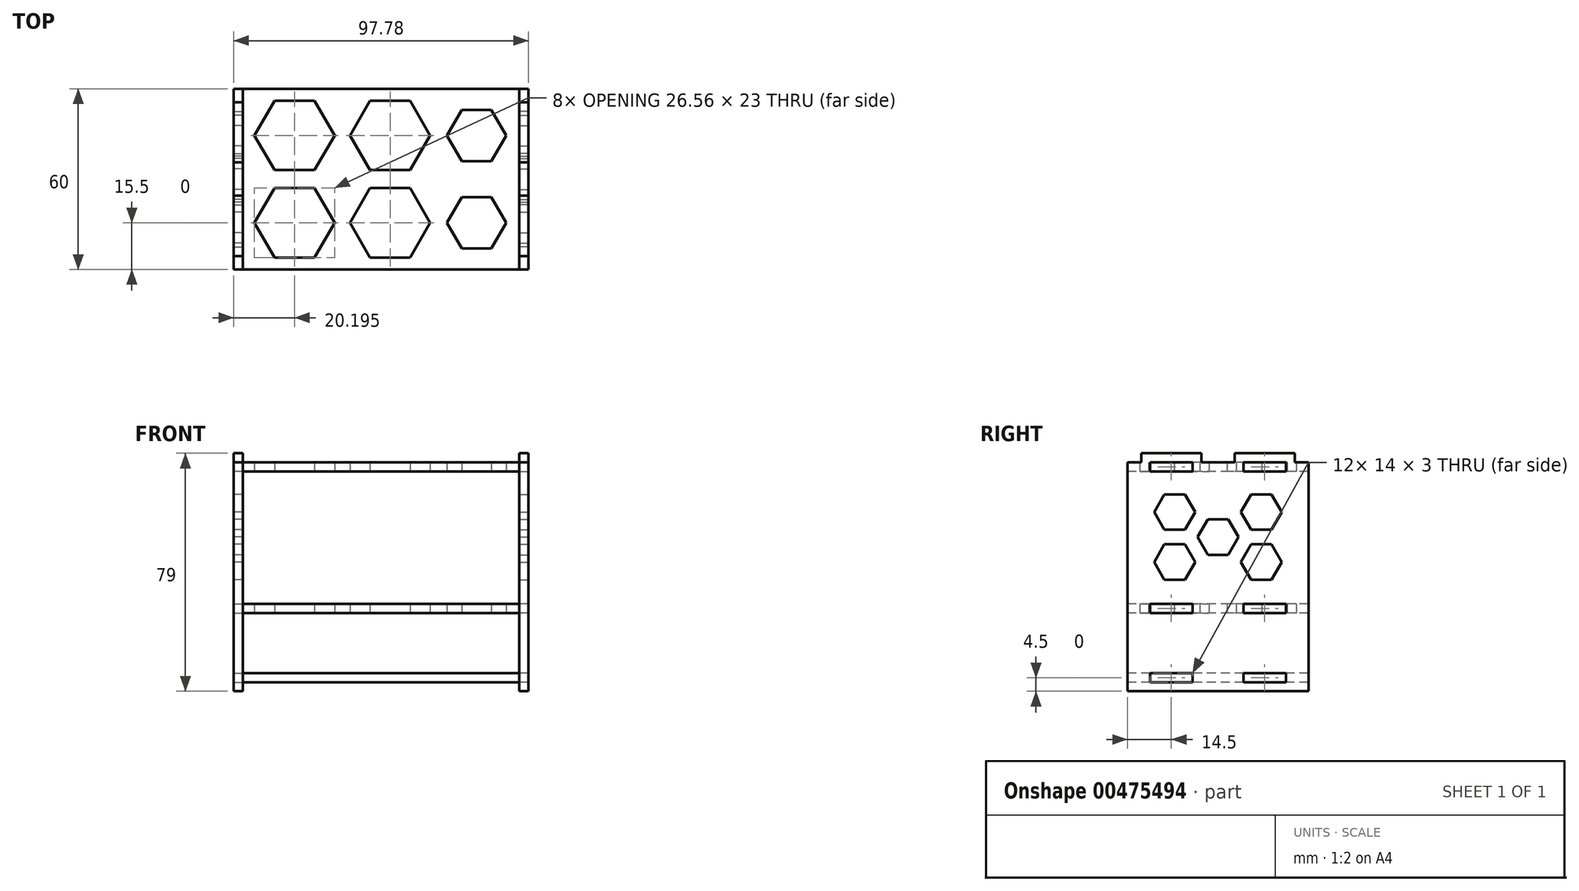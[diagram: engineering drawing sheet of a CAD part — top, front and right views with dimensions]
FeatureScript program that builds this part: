
annotation { "Feature Type Name" : "Feature", "Feature Type Description" : "" }
export const myFeature = defineFeature(function(context is Context, id is Id, definition is map)
    precondition{}
    {
        {
            assignVariable(context, id + "F0", {"name" : "x", "anyValue" : 3});
        }
        {
            var Q0;
            Q0=qCreatedBy(makeId("Top.planeOp"),FACE);
            var sketch = newSketch(context, id + "F1", { "sketchPlane" : qUnion([Q0])});
            skLineSegment(sketch, "E0.bottom", {"start": v(45.9, 30) * mm, "end": v(-45.9, 30) * mm});
            skLineSegment(sketch, "E0.top", {"start": v(45.9, -30) * mm, "end": v(-45.9, -30) * mm});
            skPoint(sketch, "E0.middle", {"position": v(0, 0) * mm});
            skCircle(sketch, "E1", {"center": v(-28.7, 14.5) * mm, "radius": 11.5 * mm, "construction": true});
            skCircle(sketch, "E2", {"center": v(3, 14.5) * mm, "radius": 11.5 * mm, "construction": true});
            skCircle(sketch, "E3", {"center": v(31.7, 14.5) * mm, "radius": 8.5 * mm, "construction": true});
            skPoint(sketch, "E4", {"position": v(-48.9, 0) * mm});
            skLineSegment(sketch, "E5", {"start": v(-48.9, 14.5) * mm, "end": v(48.9, 14.5) * mm, "construction": true});
            skLineSegment(sketch, "E6", {"start": v(-17.2, 14.5) * mm, "end": v(-8.5, 14.5) * mm, "construction": true});
            skLineSegment(sketch, "E7", {"start": v(14.5, 14.5) * mm, "end": v(23.2, 14.5) * mm, "construction": true});
            skLineSegment(sketch, "E8", {"start": v(-40.2, 14.5) * mm, "end": v(-48.9, 14.5) * mm, "construction": true});
            skLineSegment(sketch, "E9", {"start": v(40.2, 14.5) * mm, "end": v(48.9, 14.5) * mm, "construction": true});
            skLineSegment(sketch, "E10.bottom", {"start": v(-48.9, 8.5) * mm, "end": v(-45.9, 8.5) * mm});
            skLineSegment(sketch, "E10.top", {"start": v(-48.9, 22.5) * mm, "end": v(-45.9, 22.5) * mm});
            skLineSegment(sketch, "E10.left", {"start": v(-48.9, 8.5) * mm, "end": v(-48.9, 22.5) * mm});
            skLineSegment(sketch, "E11", {"start": v(-45.9, 30) * mm, "end": v(-45.9, 22.5) * mm});
            skLineSegment(sketch, "E12.MirrorCS", {"start": v(-48.9, -8.5) * mm, "end": v(-45.9, -8.5) * mm});
            skLineSegment(sketch, "E13.MirrorCS", {"start": v(-48.9, -22.5) * mm, "end": v(-45.9, -22.5) * mm});
            skLineSegment(sketch, "E14.MirrorCS", {"start": v(-48.9, -8.5) * mm, "end": v(-48.9, -22.5) * mm});
            skLineSegment(sketch, "E15.trimOffspring", {"start": v(-45.9, -22.5) * mm, "end": v(-45.9, -30) * mm});
            skPoint(sketch, "E16.MirrorCS.end.orphan", {"position": v(-45.9, -22.5) * mm});
            skPoint(sketch, "E16.MirrorCS.start.orphan", {"position": v(-45.9, -8.5) * mm});
            skLineSegment(sketch, "E17.trimOffspring", {"start": v(-45.9, 8.5) * mm, "end": v(-45.9, -8.5) * mm});
            skPoint(sketch, "E18.orphan", {"position": v(-48.9, 30) * mm});
            skPoint(sketch, "E19.orphan", {"position": v(-48.9, -30) * mm});
            skPoint(sketch, "E20.MirrorP", {"position": v(48.9, 0) * mm});
            skLineSegment(sketch, "E21.MirrorCS", {"start": v(48.9, 8.5) * mm, "end": v(48.9, 22.5) * mm});
            skLineSegment(sketch, "E22.MirrorCS", {"start": v(45.9, 8.5) * mm, "end": v(45.9, -8.5) * mm});
            skPoint(sketch, "E23.MirrorP", {"position": v(45.9, -8.5) * mm});
            skLineSegment(sketch, "E24.MirrorCS", {"start": v(48.9, 8.5) * mm, "end": v(45.9, 8.5) * mm});
            skLineSegment(sketch, "E25.MirrorCS", {"start": v(48.9, -8.5) * mm, "end": v(45.9, -8.5) * mm});
            skLineSegment(sketch, "E26.MirrorCS", {"start": v(48.9, -22.5) * mm, "end": v(45.9, -22.5) * mm});
            skPoint(sketch, "E27.MirrorP", {"position": v(45.9, -22.5) * mm});
            skLineSegment(sketch, "E28.MirrorCS", {"start": v(48.9, 22.5) * mm, "end": v(45.9, 22.5) * mm});
            skLineSegment(sketch, "E29.MirrorCS", {"start": v(48.9, -8.5) * mm, "end": v(48.9, -22.5) * mm});
            skLineSegment(sketch, "E30.MirrorCS", {"start": v(45.9, -22.5) * mm, "end": v(45.9, -30) * mm});
            skLineSegment(sketch, "E31.MirrorCS", {"start": v(45.9, 30) * mm, "end": v(45.9, 22.5) * mm});
            skPoint(sketch, "E32.orphan", {"position": v(48.9, 30) * mm});
            skPoint(sketch, "E33.orphan", {"position": v(48.9, -30) * mm});
            skLineSegment(sketch, "E34.0", {"start": v(-22.06, 26) * mm, "end": v(-15.42, 14.5) * mm});
            skLineSegment(sketch, "E34.1", {"start": v(-15.42, 14.5) * mm, "end": v(-22.06, 3) * mm});
            skLineSegment(sketch, "E34.2", {"start": v(-22.06, 3) * mm, "end": v(-35.33, 3) * mm});
            skLineSegment(sketch, "E34.3", {"start": v(-35.33, 3) * mm, "end": v(-41.97, 14.5) * mm});
            skLineSegment(sketch, "E34.4", {"start": v(-41.97, 14.5) * mm, "end": v(-35.33, 26) * mm});
            skLineSegment(sketch, "E34.5", {"start": v(-35.33, 26) * mm, "end": v(-22.06, 26) * mm});
            skPoint(sketch, "E34.0.midPoint", {"position": v(-18.74, 20.25) * mm});
            skLineSegment(sketch, "E35.0", {"start": v(9.64, 26) * mm, "end": v(16.28, 14.5) * mm});
            skLineSegment(sketch, "E35.1", {"start": v(16.28, 14.5) * mm, "end": v(9.64, 3) * mm});
            skLineSegment(sketch, "E35.2", {"start": v(9.64, 3) * mm, "end": v(-3.64, 3) * mm});
            skLineSegment(sketch, "E35.3", {"start": v(-3.64, 3) * mm, "end": v(-10.28, 14.5) * mm});
            skLineSegment(sketch, "E35.4", {"start": v(-10.28, 14.5) * mm, "end": v(-3.64, 26) * mm});
            skLineSegment(sketch, "E35.5", {"start": v(-3.64, 26) * mm, "end": v(9.64, 26) * mm});
            skPoint(sketch, "E35.0.midPoint", {"position": v(12.96, 20.25) * mm});
            skLineSegment(sketch, "E36.0", {"start": v(36.6, 23) * mm, "end": v(41.51, 14.5) * mm});
            skLineSegment(sketch, "E36.1", {"start": v(41.51, 14.5) * mm, "end": v(36.6, 6) * mm});
            skLineSegment(sketch, "E36.2", {"start": v(36.6, 6) * mm, "end": v(26.79, 6) * mm});
            skLineSegment(sketch, "E36.3", {"start": v(26.79, 6) * mm, "end": v(21.88, 14.5) * mm});
            skLineSegment(sketch, "E36.4", {"start": v(21.88, 14.5) * mm, "end": v(26.79, 23) * mm});
            skLineSegment(sketch, "E36.5", {"start": v(26.79, 23) * mm, "end": v(36.6, 23) * mm});
            skPoint(sketch, "E36.0.midPoint", {"position": v(39.06, 18.75) * mm});
            skLineSegment(sketch, "E37.MirrorCS", {"start": v(36.6, -6) * mm, "end": v(26.79, -6) * mm});
            skLineSegment(sketch, "E38.MirrorCS", {"start": v(26.79, -23) * mm, "end": v(36.6, -23) * mm});
            skLineSegment(sketch, "E39.MirrorCS", {"start": v(-22.06, -3) * mm, "end": v(-35.33, -3) * mm});
            skLineSegment(sketch, "E40.MirrorCS", {"start": v(-17.2, -14.5) * mm, "end": v(-8.5, -14.5) * mm, "construction": true});
            skLineSegment(sketch, "E41.MirrorCS", {"start": v(9.64, -3) * mm, "end": v(-3.64, -3) * mm});
            skLineSegment(sketch, "E42.MirrorCS", {"start": v(21.88, -14.5) * mm, "end": v(26.79, -23) * mm});
            skCircle(sketch, "E43.MirrorC", {"center": v(-28.7, -14.5) * mm, "radius": 11.5 * mm, "construction": true});
            skLineSegment(sketch, "E44.MirrorCS", {"start": v(9.64, -26) * mm, "end": v(16.28, -14.5) * mm});
            skLineSegment(sketch, "E45.MirrorCS", {"start": v(36.6, -23) * mm, "end": v(41.51, -14.5) * mm});
            skLineSegment(sketch, "E46.MirrorCS", {"start": v(-22.06, -26) * mm, "end": v(-15.42, -14.5) * mm});
            skCircle(sketch, "E47.MirrorC", {"center": v(3, -14.5) * mm, "radius": 11.5 * mm, "construction": true});
            skCircle(sketch, "E48.MirrorC", {"center": v(31.7, -14.5) * mm, "radius": 8.5 * mm, "construction": true});
            skLineSegment(sketch, "E49.MirrorCS", {"start": v(14.5, -14.5) * mm, "end": v(23.2, -14.5) * mm, "construction": true});
            skLineSegment(sketch, "E50.MirrorCS", {"start": v(-3.64, -3) * mm, "end": v(-10.28, -14.5) * mm});
            skLineSegment(sketch, "E51.MirrorCS", {"start": v(-3.64, -26) * mm, "end": v(9.64, -26) * mm});
            skLineSegment(sketch, "E52.MirrorCS", {"start": v(-41.97, -14.5) * mm, "end": v(-35.33, -26) * mm});
            skPoint(sketch, "E53.MirrorP", {"position": v(39.06, -18.75) * mm});
            skLineSegment(sketch, "E54.MirrorCS", {"start": v(-15.42, -14.5) * mm, "end": v(-22.06, -3) * mm});
            skLineSegment(sketch, "E55.MirrorCS", {"start": v(-35.33, -3) * mm, "end": v(-41.97, -14.5) * mm});
            skPoint(sketch, "E56.MirrorP", {"position": v(-18.74, -20.25) * mm});
            skPoint(sketch, "E57.MirrorP", {"position": v(12.96, -20.25) * mm});
            skLineSegment(sketch, "E58.MirrorCS", {"start": v(-35.33, -26) * mm, "end": v(-22.06, -26) * mm});
            skLineSegment(sketch, "E59.MirrorCS", {"start": v(-10.28, -14.5) * mm, "end": v(-3.64, -26) * mm});
            skLineSegment(sketch, "E60.MirrorCS", {"start": v(26.79, -6) * mm, "end": v(21.88, -14.5) * mm});
            skLineSegment(sketch, "E61.MirrorCS", {"start": v(16.28, -14.5) * mm, "end": v(9.64, -3) * mm});
            skLineSegment(sketch, "E62.MirrorCS", {"start": v(41.51, -14.5) * mm, "end": v(36.6, -6) * mm});
            skSolve(sketch);
        }
        {
            var Q0;
            Q0=makeQuery(id+"F1.imprint","IMPRINT",FACE,{"disambiguationData":[TD([[makeQuery(id+"F1.imprint","IMPRINT",EDGE,{"derivedFrom":sQuery(id+"F1.wireOp",EDGE,"E0.bottom")}),1.0]])]});
            extrude(context, id + "F2", {"entities" : qUnion([Q0]), "depth" : 50 * mm});
        }
        {
            var Q0;
            Q0 = qSketchRegion(id + "F1", true);
            extrude(context, id + "F3", {"entities" : qUnion([Q0]), "operationType" : NewBodyOperationType.REMOVE, "depth" : (50 - getVariable(context, 'x')) * mm});
        }
        {
            var Q0;
            Q0 = qSketchRegion(id + "F1", true);
            extrude(context, id + "F4", {"entities" : qUnion([Q0]), "depth" : (getVariable(context, 'x')) * mm});
        }
        {
            var Q0;
            Q0=makeQuery(id+"F1.imprint","IMPRINT",FACE,{"disambiguationData":[TD([[makeQuery(id+"F1.imprint","IMPRINT",EDGE,{"derivedFrom":sQuery(id+"F1.wireOp",EDGE,"E0.bottom")}),1.0]])]});
            var sketch = newSketch(context, id + "F5", { "sketchPlane" : qUnion([Q0])});
            skPoint(sketch, "E63", {"position": v(-45.9, -30) * mm});
            skLineSegment(sketch, "E64", {"start": v(-45.9, -30) * mm, "end": v(-45.9, -22.5) * mm});
            skLineSegment(sketch, "E65", {"start": v(-45.9, -22.5) * mm, "end": v(-48.9, -22.5) * mm});
            skLineSegment(sketch, "E66", {"start": v(-48.9, -22.5) * mm, "end": v(-48.9, -8.5) * mm});
            skLineSegment(sketch, "E67", {"start": v(-48.9, -8.5) * mm, "end": v(-45.9, -8.5) * mm});
            skLineSegment(sketch, "E68", {"start": v(-45.9, -8.5) * mm, "end": v(-45.9, 0) * mm});
            skLineSegment(sketch, "E69", {"start": v(-45.9, -30) * mm, "end": v(0, -30) * mm});
            skLineSegment(sketch, "E70.MirrorCS", {"start": v(45.9, -30) * mm, "end": v(45.9, -22.5) * mm});
            skLineSegment(sketch, "E71.MirrorCS", {"start": v(45.9, -22.5) * mm, "end": v(48.9, -22.5) * mm});
            skLineSegment(sketch, "E72.MirrorCS", {"start": v(48.9, -8.5) * mm, "end": v(45.9, -8.5) * mm});
            skLineSegment(sketch, "E73.MirrorCS", {"start": v(45.9, -8.5) * mm, "end": v(45.9, 0) * mm});
            skPoint(sketch, "E74.MirrorP", {"position": v(45.9, -30) * mm});
            skLineSegment(sketch, "E75.MirrorCS", {"start": v(45.9, -30) * mm, "end": v(0, -30) * mm});
            skLineSegment(sketch, "E76.MirrorCS", {"start": v(48.9, -22.5) * mm, "end": v(48.9, -8.5) * mm});
            skLineSegment(sketch, "E77.MirrorCS", {"start": v(48.9, 8.5) * mm, "end": v(45.9, 8.5) * mm});
            skLineSegment(sketch, "E78.MirrorCS", {"start": v(-45.9, 30) * mm, "end": v(-45.9, 22.5) * mm});
            skLineSegment(sketch, "E79.MirrorCS", {"start": v(-45.9, 22.5) * mm, "end": v(-48.9, 22.5) * mm});
            skLineSegment(sketch, "E80.MirrorCS", {"start": v(45.9, 22.5) * mm, "end": v(48.9, 22.5) * mm});
            skLineSegment(sketch, "E81.MirrorCS", {"start": v(-48.9, 8.5) * mm, "end": v(-45.9, 8.5) * mm});
            skLineSegment(sketch, "E82.MirrorCS", {"start": v(45.9, 30) * mm, "end": v(45.9, 22.5) * mm});
            skLineSegment(sketch, "E83.MirrorCS", {"start": v(45.9, 8.5) * mm, "end": v(45.9, 0) * mm});
            skLineSegment(sketch, "E84.MirrorCS", {"start": v(-45.9, 8.5) * mm, "end": v(-45.9, 0) * mm});
            skPoint(sketch, "E85.MirrorP", {"position": v(-45.9, 30) * mm});
            skPoint(sketch, "E86.MirrorP", {"position": v(45.9, 30) * mm});
            skLineSegment(sketch, "E87.MirrorCS", {"start": v(48.9, 22.5) * mm, "end": v(48.9, 8.5) * mm});
            skLineSegment(sketch, "E88.MirrorCS", {"start": v(45.9, 30) * mm, "end": v(0, 30) * mm});
            skLineSegment(sketch, "E89.MirrorCS", {"start": v(-48.9, 22.5) * mm, "end": v(-48.9, 8.5) * mm});
            skLineSegment(sketch, "E90.MirrorCS", {"start": v(-45.9, 30) * mm, "end": v(0, 30) * mm});
            skSolve(sketch);
        }
        {
            var Q0;
            Q0 = qSketchRegion(id + "F5", true);
            extrude(context, id + "F6", {"entities" : qUnion([Q0]), "oppositeDirection" : true, "depth" : 23 * mm});
        }
        {
            var Q0;
            Q0 = qSketchRegion(id + "F5", true);
            extrude(context, id + "F7", {"entities" : qUnion([Q0]), "operationType" : NewBodyOperationType.REMOVE, "oppositeDirection" : true, "depth" : (23 - getVariable(context, 'x')) * mm});
        }
        {
            var Q0;
            Q0=makeQuery(id+"F4.opExtrude","SWEPT_FACE",FACE,{"disambiguationData":[OSD([sQuery(id+"F1.wireOp",EDGE,"E14.MirrorCS")])]});
            var sketch = newSketch(context, id + "F8", { "sketchPlane" : qUnion([Q0])});
            skLineSegment(sketch, "E91", {"start": v(30, -23) * mm, "end": v(30, 50) * mm});
            skLineSegment(sketch, "E92", {"start": v(30, 50) * mm, "end": v(25.5, 50) * mm});
            skLineSegment(sketch, "E93", {"start": v(25.5, 50) * mm, "end": v(25.5, 53) * mm});
            skLineSegment(sketch, "E94", {"start": v(25.5, 53) * mm, "end": v(5.5, 53) * mm});
            skLineSegment(sketch, "E95", {"start": v(5.5, 53) * mm, "end": v(5.5, 50) * mm});
            skLineSegment(sketch, "E96", {"start": v(5.5, 50) * mm, "end": v(0, 50) * mm});
            skLineSegment(sketch, "E97", {"start": v(30, -23) * mm, "end": v(30, -26) * mm});
            skLineSegment(sketch, "E98", {"start": v(30, -26) * mm, "end": v(0, -26) * mm});
            skLineSegment(sketch, "E99.bottom", {"start": v(8.5, -23) * mm, "end": v(22.5, -23) * mm});
            skLineSegment(sketch, "E99.top", {"start": v(8.5, -20) * mm, "end": v(22.5, -20) * mm});
            skLineSegment(sketch, "E99.left", {"start": v(8.5, -23) * mm, "end": v(8.5, -20) * mm});
            skLineSegment(sketch, "E99.right", {"start": v(22.5, -23) * mm, "end": v(22.5, -20) * mm});
            skLineSegment(sketch, "E100.bottom", {"start": v(8.5, 0) * mm, "end": v(22.5, 0) * mm});
            skLineSegment(sketch, "E100.top", {"start": v(8.5, 3) * mm, "end": v(22.5, 3) * mm});
            skLineSegment(sketch, "E100.left", {"start": v(8.5, 0) * mm, "end": v(8.5, 3) * mm});
            skLineSegment(sketch, "E100.right", {"start": v(22.5, 0) * mm, "end": v(22.5, 3) * mm});
            skLineSegment(sketch, "E101.bottom", {"start": v(8.5, 47) * mm, "end": v(22.5, 47) * mm});
            skLineSegment(sketch, "E101.top", {"start": v(8.5, 50) * mm, "end": v(22.5, 50) * mm});
            skLineSegment(sketch, "E101.left", {"start": v(8.5, 47) * mm, "end": v(8.5, 50) * mm});
            skLineSegment(sketch, "E101.right", {"start": v(22.5, 47) * mm, "end": v(22.5, 50) * mm});
            skLineSegment(sketch, "E102.MirrorCS", {"start": v(-22.5, 0) * mm, "end": v(-22.5, 3) * mm});
            skLineSegment(sketch, "E103.MirrorCS", {"start": v(-8.5, 0) * mm, "end": v(-8.5, 3) * mm});
            skLineSegment(sketch, "E104.MirrorCS", {"start": v(-8.5, 0) * mm, "end": v(-22.5, 0) * mm});
            skLineSegment(sketch, "E105.MirrorCS", {"start": v(-8.5, 47) * mm, "end": v(-8.5, 50) * mm});
            skLineSegment(sketch, "E106.MirrorCS", {"start": v(-5.5, 53) * mm, "end": v(-5.5, 50) * mm});
            skLineSegment(sketch, "E107.MirrorCS", {"start": v(-8.5, -23) * mm, "end": v(-8.5, -20) * mm});
            skLineSegment(sketch, "E108.MirrorCS", {"start": v(-22.5, -23) * mm, "end": v(-22.5, -20) * mm});
            skLineSegment(sketch, "E109.MirrorCS", {"start": v(-30, 50) * mm, "end": v(-25.5, 50) * mm});
            skLineSegment(sketch, "E110.MirrorCS", {"start": v(-25.5, 50) * mm, "end": v(-25.5, 53) * mm});
            skLineSegment(sketch, "E111.MirrorCS", {"start": v(-22.5, 47) * mm, "end": v(-22.5, 50) * mm});
            skLineSegment(sketch, "E112.MirrorCS", {"start": v(-30, -23) * mm, "end": v(-30, -26) * mm});
            skLineSegment(sketch, "E113.MirrorCS", {"start": v(-25.5, 53) * mm, "end": v(-5.5, 53) * mm});
            skLineSegment(sketch, "E114.MirrorCS", {"start": v(-5.5, 50) * mm, "end": v(0, 50) * mm});
            skLineSegment(sketch, "E115.MirrorCS", {"start": v(-8.5, -20) * mm, "end": v(-22.5, -20) * mm});
            skLineSegment(sketch, "E116.MirrorCS", {"start": v(-8.5, 47) * mm, "end": v(-22.5, 47) * mm});
            skLineSegment(sketch, "E117.MirrorCS", {"start": v(-30, -23) * mm, "end": v(-30, 50) * mm});
            skLineSegment(sketch, "E118.MirrorCS", {"start": v(-8.5, -23) * mm, "end": v(-22.5, -23) * mm});
            skLineSegment(sketch, "E119.MirrorCS", {"start": v(-8.5, 3) * mm, "end": v(-22.5, 3) * mm});
            skLineSegment(sketch, "E120.MirrorCS", {"start": v(-30, -26) * mm, "end": v(0, -26) * mm});
            skLineSegment(sketch, "E121.MirrorCS", {"start": v(-8.5, 50) * mm, "end": v(-22.5, 50) * mm});
            skCircle(sketch, "E122.cCircle", {"center": v(0, 25.17) * mm, "radius": 6.8 * mm, "construction": true});
            skLineSegment(sketch, "E122.0", {"start": v(6.8, 25.17) * mm, "end": v(3.4, 19.29) * mm});
            skLineSegment(sketch, "E122.1", {"start": v(3.4, 19.29) * mm, "end": v(-3.4, 19.29) * mm});
            skLineSegment(sketch, "E122.2", {"start": v(-3.4, 19.29) * mm, "end": v(-6.8, 25.17) * mm});
            skLineSegment(sketch, "E122.3", {"start": v(-6.8, 25.17) * mm, "end": v(-3.4, 31.06) * mm});
            skLineSegment(sketch, "E122.4", {"start": v(-3.4, 31.06) * mm, "end": v(3.4, 31.06) * mm});
            skLineSegment(sketch, "E122.5", {"start": v(3.4, 31.06) * mm, "end": v(6.8, 25.17) * mm});
            skCircle(sketch, "E123.cCircle", {"center": v(-14.38, 33.48) * mm, "radius": 6.8 * mm, "construction": true});
            skLineSegment(sketch, "E123.0", {"start": v(-7.59, 33.48) * mm, "end": v(-10.99, 27.6) * mm});
            skLineSegment(sketch, "E123.1", {"start": v(-10.99, 27.6) * mm, "end": v(-17.78, 27.6) * mm});
            skLineSegment(sketch, "E123.2", {"start": v(-17.78, 27.6) * mm, "end": v(-21.18, 33.48) * mm});
            skLineSegment(sketch, "E123.3", {"start": v(-21.18, 33.48) * mm, "end": v(-17.78, 39.36) * mm});
            skLineSegment(sketch, "E123.4", {"start": v(-17.78, 39.36) * mm, "end": v(-10.99, 39.36) * mm});
            skLineSegment(sketch, "E123.5", {"start": v(-10.99, 39.36) * mm, "end": v(-7.59, 33.48) * mm});
            skCircle(sketch, "E124.cCircle", {"center": v(14.38, 33.48) * mm, "radius": 6.8 * mm, "construction": true});
            skLineSegment(sketch, "E124.0", {"start": v(21.18, 33.48) * mm, "end": v(17.78, 27.6) * mm});
            skLineSegment(sketch, "E124.1", {"start": v(17.78, 27.6) * mm, "end": v(10.99, 27.6) * mm});
            skLineSegment(sketch, "E124.2", {"start": v(10.99, 27.6) * mm, "end": v(7.59, 33.48) * mm});
            skLineSegment(sketch, "E124.3", {"start": v(7.59, 33.48) * mm, "end": v(10.99, 39.36) * mm});
            skLineSegment(sketch, "E124.4", {"start": v(10.99, 39.36) * mm, "end": v(17.78, 39.36) * mm});
            skLineSegment(sketch, "E124.5", {"start": v(17.78, 39.36) * mm, "end": v(21.18, 33.48) * mm});
            skCircle(sketch, "E125.cCircle", {"center": v(-14.38, 16.87) * mm, "radius": 6.8 * mm, "construction": true});
            skLineSegment(sketch, "E125.0", {"start": v(-7.59, 16.87) * mm, "end": v(-10.99, 10.98) * mm});
            skLineSegment(sketch, "E125.1", {"start": v(-10.99, 10.98) * mm, "end": v(-17.78, 10.98) * mm});
            skLineSegment(sketch, "E125.2", {"start": v(-17.78, 10.98) * mm, "end": v(-21.18, 16.87) * mm});
            skLineSegment(sketch, "E125.3", {"start": v(-21.18, 16.87) * mm, "end": v(-17.78, 22.75) * mm});
            skLineSegment(sketch, "E125.4", {"start": v(-17.78, 22.75) * mm, "end": v(-10.99, 22.75) * mm});
            skLineSegment(sketch, "E125.5", {"start": v(-10.99, 22.75) * mm, "end": v(-7.59, 16.87) * mm});
            skCircle(sketch, "E126.cCircle", {"center": v(14.38, 16.87) * mm, "radius": 6.8 * mm, "construction": true});
            skLineSegment(sketch, "E126.0", {"start": v(21.18, 16.87) * mm, "end": v(17.78, 10.98) * mm});
            skLineSegment(sketch, "E126.1", {"start": v(17.78, 10.98) * mm, "end": v(10.99, 10.98) * mm});
            skLineSegment(sketch, "E126.2", {"start": v(10.99, 10.98) * mm, "end": v(7.59, 16.87) * mm});
            skLineSegment(sketch, "E126.3", {"start": v(7.59, 16.87) * mm, "end": v(10.99, 22.75) * mm});
            skLineSegment(sketch, "E126.4", {"start": v(10.99, 22.75) * mm, "end": v(17.78, 22.75) * mm});
            skLineSegment(sketch, "E126.5", {"start": v(17.78, 22.75) * mm, "end": v(21.18, 16.87) * mm});
            skLineSegment(sketch, "E127", {"start": v(-17.78, 39.36) * mm, "end": v(21.18, 16.87) * mm, "construction": true});
            skLineSegment(sketch, "E128", {"start": v(-21.18, 16.87) * mm, "end": v(17.78, 39.36) * mm, "construction": true});
            skSolve(sketch);
        }
        {
            var Q0;
            Q0 = qSketchRegion(id + "F8", true);
            extrude(context, id + "F9", {"entities" : qUnion([Q0]), "oppositeDirection" : true, "depth" : (getVariable(context, 'x')) * mm});
        }
        {
            var Q0;
            Q0=makeQuery(id+"F9.opExtrude","SWEPT_BODY",BODY,{"disambiguationData":[OSD([sQuery(id+"F8.wireOp",EDGE,"E91"),sQuery(id+"F8.wireOp",EDGE,"E92"),sQuery(id+"F8.wireOp",EDGE,"E93"),sQuery(id+"F8.wireOp",EDGE,"E94"),sQuery(id+"F8.wireOp",EDGE,"E95"),sQuery(id+"F8.wireOp",EDGE,"E96"),sQuery(id+"F8.wireOp",EDGE,"E97"),sQuery(id+"F8.wireOp",EDGE,"E98"),sQuery(id+"F8.wireOp",EDGE,"E99.bottom"),sQuery(id+"F8.wireOp",EDGE,"E99.top"),sQuery(id+"F8.wireOp",EDGE,"E99.left"),sQuery(id+"F8.wireOp",EDGE,"E99.right"),sQuery(id+"F8.wireOp",EDGE,"E100.bottom"),sQuery(id+"F8.wireOp",EDGE,"E100.top"),sQuery(id+"F8.wireOp",EDGE,"E100.left"),sQuery(id+"F8.wireOp",EDGE,"E100.right"),sQuery(id+"F8.wireOp",EDGE,"E101.bottom"),sQuery(id+"F8.wireOp",EDGE,"E101.top"),sQuery(id+"F8.wireOp",EDGE,"E101.left"),sQuery(id+"F8.wireOp",EDGE,"E101.right"),sQuery(id+"F8.wireOp",EDGE,"E102.MirrorCS"),sQuery(id+"F8.wireOp",EDGE,"E103.MirrorCS"),sQuery(id+"F8.wireOp",EDGE,"E104.MirrorCS"),sQuery(id+"F8.wireOp",EDGE,"E105.MirrorCS"),sQuery(id+"F8.wireOp",EDGE,"E106.MirrorCS"),sQuery(id+"F8.wireOp",EDGE,"E107.MirrorCS"),sQuery(id+"F8.wireOp",EDGE,"E108.MirrorCS"),sQuery(id+"F8.wireOp",EDGE,"E109.MirrorCS"),sQuery(id+"F8.wireOp",EDGE,"E110.MirrorCS"),sQuery(id+"F8.wireOp",EDGE,"E111.MirrorCS"),sQuery(id+"F8.wireOp",EDGE,"E112.MirrorCS"),sQuery(id+"F8.wireOp",EDGE,"E113.MirrorCS"),sQuery(id+"F8.wireOp",EDGE,"E114.MirrorCS"),sQuery(id+"F8.wireOp",EDGE,"E115.MirrorCS"),sQuery(id+"F8.wireOp",EDGE,"E116.MirrorCS"),sQuery(id+"F8.wireOp",EDGE,"E117.MirrorCS"),sQuery(id+"F8.wireOp",EDGE,"E118.MirrorCS"),sQuery(id+"F8.wireOp",EDGE,"E119.MirrorCS"),sQuery(id+"F8.wireOp",EDGE,"E120.MirrorCS"),sQuery(id+"F8.wireOp",EDGE,"E121.MirrorCS"),sQuery(id+"F8.wireOp",EDGE,"E122.0"),sQuery(id+"F8.wireOp",EDGE,"E122.1"),sQuery(id+"F8.wireOp",EDGE,"E122.2"),sQuery(id+"F8.wireOp",EDGE,"E122.3"),sQuery(id+"F8.wireOp",EDGE,"E122.4"),sQuery(id+"F8.wireOp",EDGE,"E122.5"),sQuery(id+"F8.wireOp",EDGE,"E123.0"),sQuery(id+"F8.wireOp",EDGE,"E123.1"),sQuery(id+"F8.wireOp",EDGE,"E123.2"),sQuery(id+"F8.wireOp",EDGE,"E123.3"),sQuery(id+"F8.wireOp",EDGE,"E123.4"),sQuery(id+"F8.wireOp",EDGE,"E123.5"),sQuery(id+"F8.wireOp",EDGE,"E124.0"),sQuery(id+"F8.wireOp",EDGE,"E124.1"),sQuery(id+"F8.wireOp",EDGE,"E124.2"),sQuery(id+"F8.wireOp",EDGE,"E124.3"),sQuery(id+"F8.wireOp",EDGE,"E124.4"),sQuery(id+"F8.wireOp",EDGE,"E124.5"),sQuery(id+"F8.wireOp",EDGE,"E125.0"),sQuery(id+"F8.wireOp",EDGE,"E125.1"),sQuery(id+"F8.wireOp",EDGE,"E125.2"),sQuery(id+"F8.wireOp",EDGE,"E125.3"),sQuery(id+"F8.wireOp",EDGE,"E125.4"),sQuery(id+"F8.wireOp",EDGE,"E125.5"),sQuery(id+"F8.wireOp",EDGE,"E126.0"),sQuery(id+"F8.wireOp",EDGE,"E126.1"),sQuery(id+"F8.wireOp",EDGE,"E126.2"),sQuery(id+"F8.wireOp",EDGE,"E126.3"),sQuery(id+"F8.wireOp",EDGE,"E126.4"),sQuery(id+"F8.wireOp",EDGE,"E126.5")])]});
            var Q1;
            Q1=qCreatedBy(makeId("Right.planeOp"),FACE);
            mirror(context, id + "F10", {"entities" : qUnion([Q0]), "mirrorPlane" : qUnion([Q1])});
        }
    });
